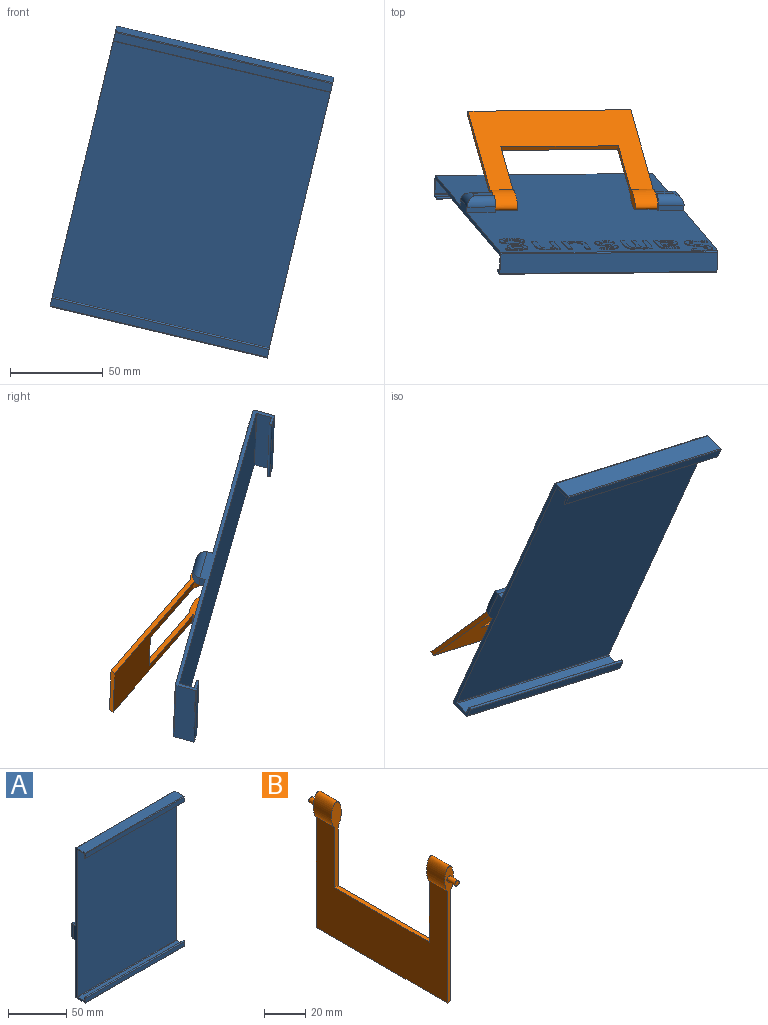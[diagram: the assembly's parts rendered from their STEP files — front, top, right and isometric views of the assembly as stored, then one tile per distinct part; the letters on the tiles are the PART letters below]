
ASSEMBLY  parts=2 mates=1
PART A: 200 faces, bbox 120x19.9x158 mm
  f0: plane 157.09x120mm, normal (0,1,0), area 17591.8mm2, adj f1,f2,f19,f20,f23,f24,f25,f26
  f1: plane 15.75x3mm, normal (0,0,1), area 47.3mm2, adj f0,f24,f29,f34
  f2: plane 15.75x3mm, normal (0,0,-1), area 47.3mm2, adj f0,f24,f29,f36
  f3: plane 9.25x5mm, normal (0,1,0), area 46.2mm2, adj f28,f37,f38,f39
  f4: plane 120x4.78mm, normal (0,-1,0), area 573.4mm2, adj f5,f22,f23,f24
  f5: cylinder r=0.88mm len=120mm, axis (-1,0,0), area 216.3mm2, adj f4,f6,f23,f24
  f6: plane 120x3.22mm, normal (0,1,0), area 386.9mm2, adj f5,f7,f23,f24
  f7: cylinder r=0.5mm len=120mm, axis (-1,0,0), area 94.2mm2, adj f6,f8,f23,f24
  f8: plane 120x7.4mm, normal (0,0,-1), area 888mm2, adj f7,f9,f23,f24
  f9: cylinder r=0.5mm len=120mm, axis (-1,0,0), area 94.2mm2, adj f8,f10,f23,f24
  f10: plane 154x120mm, normal (0,-1,0), area 18480mm2, adj f9,f11,f23,f24
  f11: cylinder r=0.5mm len=120mm, axis (-1,0,0), area 94.2mm2, adj f10,f12,f23,f24
  f12: plane 120x7.4mm, normal (0,0,1), area 888mm2, adj f11,f13,f23,f24
  f13: cylinder r=0.5mm len=120mm, axis (-1,0,0), area 94.2mm2, adj f12,f14,f23,f24
  f14: plane 120x3.02mm, normal (0,1,0), area 361.8mm2, adj f13,f15,f23,f24
  f15: cylinder r=0.76mm len=120mm, axis (-1,0,0), area 255mm2, adj f14,f16,f23,f24
  f16: plane 120x4.48mm, normal (0,-1,0), area 537.4mm2, adj f15,f17,f23,f24
  f17: cylinder r=0.5mm len=120mm, axis (-1,0,0), area 94.2mm2, adj f16,f18,f23,f24
  f18: plane 120x10.9mm, normal (0,0,-1), area 1308mm2, adj f17,f19,f23,f24
  f19: cylinder r=0.5mm len=120mm, axis (-1,0,0), area 94.2mm2, adj f0,f18,f23,f24
  f20: cylinder r=0.5mm len=120mm, axis (-1,0,0), area 94.2mm2, adj f0,f21,f23,f24,f61
  f21: plane 120x10.9mm, normal (0,0,1), area 1308mm2, adj f20,f22,f23,f24
  f22: cylinder r=0.5mm len=120mm, axis (-1,0,0), area 94.2mm2, adj f4,f21,f23,f24
  f23: plane 158x14.9mm, normal (1,0,0), area 402.7mm2, adj f0,f4,f5,f6,f7,f8,f9,f10
  f24: plane 158x14.9mm, normal (-1,0,0), area 402.7mm2, adj f0,f1,f2,f4,f5,f6,f7,f8
  f25: plane 14.25x3mm, normal (0,0,1), area 42.7mm2, adj f0,f23,f28,f37
  f26: plane 14.25x3mm, normal (0,0,-1), area 42.7mm2, adj f0,f23,f28,f39
  f27: plane 10.75x5mm, normal (0,1,0), area 53.8mm2, adj f29,f34,f35,f36
  f28: plane 15x8mm, normal (-1,0,0), area 99.6mm2, adj f0,f3,f25,f26,f30,f37,f39
  f29: plane 15x8mm, normal (1,0,0), area 99.6mm2, adj f0,f1,f2,f27,f32,f34,f36
  f30: cylinder r=1.75mm len=6mm, axis (-1,0,0), area 66mm2, adj f28,f31
  f31: plane 3.5x3.5mm, normal (-1,0,0), area 9.6mm2, adj f30
  f32: cylinder r=1.75mm len=6mm, axis (1,0,0), area 66mm2, adj f29,f33
  f33: plane 3.5x3.5mm, normal (1,0,0), area 9.6mm2, adj f32
  f34: cylinder r=5mm len=15.75mm, axis (-1,0,0), area 109.4mm2, adj f1,f27,f29,f35
  f35: cylinder r=5mm len=15mm, axis (0,0,1), area 89.3mm2, adj f24,f27,f34,f36
  f36: cylinder r=5mm len=15.75mm, axis (1,0,0), area 109.4mm2, adj f2,f27,f29,f35
  f37: cylinder r=5mm len=14.25mm, axis (-1,0,0), area 97.6mm2, adj f3,f25,f28,f38
  f38: cylinder r=5mm len=15mm, axis (0,0,-1), area 89.3mm2, adj f3,f23,f37,f39
  f39: cylinder r=5mm len=14.25mm, axis (1,0,0), area 97.6mm2, adj f3,f26,f28,f38
  f40: extruded ~4.8x1.34mm, area 2.5mm2, adj f0,f41,f59,f60,f61
  f41: extruded ~3.71x1.75mm, area 2.1mm2, adj f0,f40,f42,f60
  f42: extruded ~3.59x1.23mm, area 1.9mm2, adj f0,f41,f43,f60
  f43: extruded ~4.07x2.38mm, area 2.4mm2, adj f0,f42,f44,f60
  f44: extruded ~3.89x1.81mm, area 2.2mm2, adj f0,f43,f45,f60
  f45: extruded ~2.18x0.96mm, area 1.2mm2, adj f0,f44,f46,f60
  f46: extruded ~4.77x3.27mm, area 3.3mm2, adj f0,f45,f47,f60
  f47: extruded ~5.64x1.17mm, area 2.9mm2, adj f0,f46,f48,f60
  f48: plane 2.42x0.5mm, normal (1,0,0), area 1.2mm2, adj f0,f47,f49,f60
  f49: extruded ~5.64x0.94mm, area 2.9mm2, adj f0,f48,f50,f60
  f50: extruded ~5.36x1.49mm, area 2.8mm2, adj f0,f49,f51,f60
  f51: extruded ~4.11x1.89mm, area 2.3mm2, adj f0,f50,f52,f60
  f52: extruded ~3.28x1.12mm, area 1.8mm2, adj f0,f51,f53,f60
  f53: extruded ~4.47x2.47mm, area 2.6mm2, adj f0,f52,f54,f60
  f54: extruded ~3.69x1.81mm, area 2.1mm2, adj f0,f53,f55,f60
  f55: extruded ~2.23x0.89mm, area 1.2mm2, adj f0,f54,f56,f60
  f56: extruded ~3.99x2.85mm, area 2.8mm2, adj f0,f55,f57,f60
  f57: extruded ~4.9x1.06mm, area 2.5mm2, adj f0,f56,f58,f60
  f58: plane 2.24x0.87mm, normal (-0.93,0,-0.36), area 1.2mm2, adj f0,f57,f59,f60
  f59: extruded ~5.67x1.06mm, area 2.9mm2, adj f0,f40,f58,f60,f61
  f60: plane 20.48x12.89mm, normal (0,1,0), area 100mm2, adj f40,f41,f42,f43,f44,f45,f46,f47
  f61: plane 3.67x0.13mm, normal (0,-1,0), area 0.3mm2, adj f20,f40,f59
  f62: plane 2.21x0.5mm, normal (-0.04,0,-1), area 1.1mm2, adj f63,f85,f86,f87
  f63: plane 1.35x0.5mm, normal (1,0,0), area 0.7mm2, adj f62,f64,f86,f87
  f64: extruded ~3.13x1.19mm, area 1.7mm2, adj f63,f65,f86,f87
  f65: extruded ~3.19x1.11mm, area 1.7mm2, adj f64,f66,f86,f87
  f66: extruded ~2.72x2.42mm, area 2.1mm2, adj f65,f67,f86,f87
  f67: extruded ~2.23x1.12mm, area 1.3mm2, adj f66,f85,f86,f87
  f68: plane 2.07x0.51mm, normal (0.97,0,-0.24), area 1.1mm2, adj f0,f69,f84,f86
  f69: plane 1.78x0.5mm, normal (0,0,-1), area 0.9mm2, adj f0,f68,f70,f86
  f70: plane 10.25x0.5mm, normal (-1,0,0), area 5.1mm2, adj f0,f69,f71,f86
  f71: extruded ~3.8x1.38mm, area 2.1mm2, adj f0,f70,f72,f86
  f72: extruded ~4.47x1.19mm, area 2.4mm2, adj f0,f71,f73,f86
  f73: extruded ~5.22x1.31mm, area 2.7mm2, adj f0,f72,f74,f86
  f74: plane 1.87x0.86mm, normal (0.91,0,-0.42), area 1mm2, adj f0,f73,f75,f86
  f75: extruded ~4.47x1.12mm, area 2.3mm2, adj f0,f74,f76,f86
  f76: extruded ~3.32x3.22mm, area 2.7mm2, adj f0,f75,f77,f86
  f77: plane 0.94x0.5mm, normal (1,0,0), area 0.5mm2, adj f0,f76,f78,f86
  f78: plane 2.76x0.5mm, normal (0.03,0,1), area 1.4mm2, adj f0,f77,f79,f86
  f79: extruded ~6.95x4.74mm, area 4.7mm2, adj f0,f78,f80,f86
  f80: extruded ~3.28x1.26mm, area 1.8mm2, adj f0,f79,f81,f86
  f81: extruded ~3.48x1.17mm, area 1.9mm2, adj f0,f80,f82,f86
  f82: extruded ~2.85x0.51mm, area 1.5mm2, adj f0,f81,f83,f86
  f83: extruded ~2.15x1.83mm, area 1.4mm2, adj f0,f82,f84,f86
  f84: plane 0.5x0.11mm, normal (0,0,-1), area 0.1mm2, adj f0,f68,f83,f86
  f85: extruded ~3.79x0.84mm, area 2mm2, adj f62,f67,f86,f87
  f86: plane 15.51x12.14mm, normal (0,1,0), area 95.3mm2, adj f62,f63,f64,f65,f66,f67,f68,f69
  f87: plane 7.11x5.58mm, normal (0,1,0), area 32mm2, adj f62,f63,f64,f65,f66,f67,f85
  f88: plane 9.63x0.5mm, normal (1,0,0), area 4.8mm2, adj f0,f89,f112,f113
  f89: plane 2.21x0.5mm, normal (0,0,-1), area 1.1mm2, adj f0,f88,f90,f113
  f90: plane 9.77x0.5mm, normal (-1,0,0), area 4.9mm2, adj f0,f89,f91,f113
  f91: extruded ~4.2x0.79mm, area 2.2mm2, adj f0,f90,f92,f113
  f92: extruded ~2.53x1.26mm, area 1.5mm2, adj f0,f91,f93,f113
  f93: extruded ~2.98x2.48mm, area 2.1mm2, adj f0,f92,f94,f113
  f94: plane 0.5x0.08mm, normal (0,0,1), area 0mm2, adj f0,f93,f95,f113
  f95: extruded ~2.9x2.48mm, area 2.1mm2, adj f0,f94,f96,f113
  f96: extruded ~2.74x2.29mm, area 1.9mm2, adj f0,f95,f97,f113
  f97: plane 0.5x0.14mm, normal (0,0,1), area 0.1mm2, adj f0,f96,f98,f113
  f98: plane 2.01x0.5mm, normal (-0.98,0,0.18), area 1mm2, adj f0,f97,f99,f113
  f99: plane 1.73x0.5mm, normal (0,0,1), area 0.9mm2, adj f0,f98,f100,f113
  f100: plane 14.96x0.5mm, normal (1,0,0), area 7.5mm2, adj f0,f99,f101,f113
  f101: plane 2.21x0.5mm, normal (0,0,-1), area 1.1mm2, adj f0,f100,f102,f113
  f102: plane 7.75x0.5mm, normal (-1,0,0), area 3.9mm2, adj f0,f101,f103,f113
  f103: extruded ~4.34x0.5mm, area 2.2mm2, adj f0,f102,f104,f113
  f104: extruded ~1.63x1.08mm, area 1mm2, adj f0,f103,f105,f113
  f105: extruded ~3.54x1.7mm, area 2.2mm2, adj f0,f104,f106,f113
  f106: plane 9.63x0.5mm, normal (1,0,0), area 4.8mm2, adj f0,f105,f107,f113
  f107: plane 2.19x0.5mm, normal (0,0,-1), area 1.1mm2, adj f0,f106,f108,f113
  f108: plane 8.26x0.5mm, normal (-1,0,0), area 4.1mm2, adj f0,f107,f109,f113
  f109: extruded ~3.79x0.54mm, area 1.9mm2, adj f0,f108,f110,f113
  f110: extruded ~1.72x1.13mm, area 1.1mm2, adj f0,f109,f111,f113
  f111: extruded ~1.21x0.78mm, area 0.8mm2, adj f0,f110,f112,f113
  f112: extruded ~2.77x0.5mm, area 1.4mm2, adj f0,f88,f111,f113
  f113: plane 15.23x14.26mm, normal (0,1,0), area 111.6mm2, adj f88,f89,f90,f91,f92,f93,f94,f95
  f114: plane 2.26x0.5mm, normal (1,0,0), area 1.1mm2, adj f0,f115,f133,f134
  f115: extruded ~5.11x0.94mm, area 2.6mm2, adj f0,f114,f116,f134
  f116: extruded ~4.51x1.17mm, area 2.4mm2, adj f0,f115,f117,f134
  f117: extruded ~3.21x1.59mm, area 1.9mm2, adj f0,f116,f118,f134
  f118: extruded ~2.49x0.95mm, area 1.4mm2, adj f0,f117,f119,f134
  f119: extruded ~3.82x2.06mm, area 2.2mm2, adj f0,f118,f120,f134
  f120: extruded ~3.17x1.39mm, area 1.7mm2, adj f0,f119,f121,f134
  f121: extruded ~1.33x0.69mm, area 0.8mm2, adj f0,f120,f122,f134
  f122: extruded ~3.22x1.81mm, area 2.1mm2, adj f0,f121,f123,f134
  f123: extruded ~4.35x0.98mm, area 2.2mm2, adj f0,f122,f124,f134
  f124: plane 2.03x0.82mm, normal (-0.93,0,-0.37), area 1.1mm2, adj f0,f123,f125,f134
  f125: extruded ~5.03x1.01mm, area 2.6mm2, adj f0,f124,f126,f134
  f126: extruded ~4.21x1.06mm, area 2.2mm2, adj f0,f125,f127,f134
  f127: extruded ~2.91x1.52mm, area 1.7mm2, adj f0,f126,f128,f134
  f128: extruded ~2.33x0.83mm, area 1.3mm2, adj f0,f127,f129,f134
  f129: extruded ~4x2.17mm, area 2.3mm2, adj f0,f128,f130,f134
  f130: extruded ~3.08x1.44mm, area 1.7mm2, adj f0,f129,f131,f134
  f131: extruded ~1.35x0.67mm, area 0.8mm2, adj f0,f130,f132,f134
  f132: extruded ~3.75x2.21mm, area 2.4mm2, adj f0,f131,f133,f134
  f133: extruded ~5.04x1.17mm, area 2.6mm2, adj f0,f114,f132,f134
  f134: plane 15.51x11.21mm, normal (0,1,0), area 76.9mm2, adj f114,f115,f116,f117,f118,f119,f120,f121
  f135: plane 2x0.5mm, normal (0.98,0,-0.18), area 1mm2, adj f0,f136,f148,f149
  f136: plane 2.01x0.5mm, normal (0,0,-1), area 1mm2, adj f0,f135,f137,f149
  f137: plane 14.96x0.5mm, normal (-1,0,0), area 7.5mm2, adj f0,f136,f138,f149
  f138: plane 2.48x0.5mm, normal (0,0,1), area 1.2mm2, adj f0,f137,f139,f149
  f139: plane 7.76x0.5mm, normal (1,0,0), area 3.9mm2, adj f0,f138,f140,f149
  f140: extruded ~4.15x1.01mm, area 2.2mm2, adj f0,f139,f141,f149
  f141: extruded ~3.2x1.26mm, area 1.8mm2, adj f0,f140,f142,f149
  f142: extruded ~3.54x3.21mm, area 2.7mm2, adj f0,f141,f143,f149
  f143: plane 9.63x0.5mm, normal (-1,0,0), area 4.8mm2, adj f0,f142,f144,f149
  f144: plane 2.48x0.5mm, normal (0,0,1), area 1.2mm2, adj f0,f143,f145,f149
  f145: plane 9.77x0.5mm, normal (1,0,0), area 4.9mm2, adj f0,f144,f146,f149
  f146: extruded ~5.47x5.33mm, area 4.4mm2, adj f0,f145,f147,f149
  f147: extruded ~4.55x2.28mm, area 2.7mm2, adj f0,f146,f148,f149
  f148: plane 0.5x0.14mm, normal (0,0,-1), area 0.1mm2, adj f0,f135,f147,f149
  f149: plane 15.23x12.39mm, normal (0,1,0), area 87.3mm2, adj f135,f136,f137,f138,f139,f140,f141,f142
  f150: plane 9.63x0.5mm, normal (1,0,0), area 4.8mm2, adj f0,f151,f162,f163
  f151: plane 2.48x0.5mm, normal (0,0,-1), area 1.2mm2, adj f0,f150,f152,f163
  f152: plane 9.77x0.5mm, normal (-1,0,0), area 4.9mm2, adj f0,f151,f153,f163
  f153: extruded ~5.46x5.3mm, area 4.4mm2, adj f0,f152,f154,f163
  f154: extruded ~4.58x2.29mm, area 2.7mm2, adj f0,f153,f155,f163
  f155: plane 0.5x0.14mm, normal (0,0,1), area 0.1mm2, adj f0,f154,f156,f163
  f156: plane 2.01x0.5mm, normal (-0.98,0,0.18), area 1mm2, adj f0,f155,f157,f163
  f157: plane 2x0.5mm, normal (0,0,1), area 1mm2, adj f0,f156,f158,f163
  f158: plane 14.96x0.5mm, normal (1,0,0), area 7.5mm2, adj f0,f157,f159,f163
  f159: plane 2.48x0.5mm, normal (0,0,-1), area 1.2mm2, adj f0,f158,f160,f163
  f160: plane 7.75x0.5mm, normal (-1,0,0), area 3.9mm2, adj f0,f159,f161,f163
  f161: extruded ~5.42x4.18mm, area 3.9mm2, adj f0,f160,f162,f163
  f162: extruded ~3.54x3.24mm, area 2.8mm2, adj f0,f150,f161,f163
  f163: plane 15.23x12.39mm, normal (0,1,0), area 87.6mm2, adj f150,f151,f152,f153,f154,f155,f156,f157
  f164: plane 2.56x0.5mm, normal (0,0,-1), area 1.3mm2, adj f165,f196,f197,f198
  f165: extruded ~2.7x0.5mm, area 1.4mm2, adj f164,f166,f197,f198
  f166: extruded ~1.61x0.68mm, area 0.9mm2, adj f165,f167,f197,f198
  f167: extruded ~5.38x3.04mm, area 3.5mm2, adj f166,f168,f197,f198
  f168: extruded ~3.69x2.37mm, area 2.5mm2, adj f167,f196,f197,f198
  f169: extruded ~3.13x3.04mm, area 2.5mm2, adj f170,f194,f197,f199
  f170: extruded ~3.09x3.09mm, area 2.5mm2, adj f169,f171,f197,f199
  f171: extruded ~3.3x3.07mm, area 2.6mm2, adj f170,f194,f197,f199
  f172: plane 1.54x0.5mm, normal (-1,0,0), area 0.8mm2, adj f0,f173,f195,f197
  f173: plane 5.15x0.5mm, normal (0,0,1), area 2.6mm2, adj f0,f172,f174,f197
  f174: extruded ~2.04x0.5mm, area 1mm2, adj f0,f173,f175,f197
  f175: extruded ~4.14x1.34mm, area 2.2mm2, adj f0,f174,f176,f197
  f176: extruded ~3.82x1.45mm, area 2.1mm2, adj f0,f175,f177,f197
  f177: extruded ~2.54x0.69mm, area 1.3mm2, adj f0,f176,f178,f197
  f178: extruded ~1.91x1.67mm, area 1.3mm2, adj f0,f177,f179,f197
  f179: extruded ~2.62x1.81mm, area 1.7mm2, adj f0,f178,f180,f197
  f180: extruded ~2.1x1.31mm, area 1.3mm2, adj f0,f179,f181,f197
  f181: extruded ~3.68x3.27mm, area 2.7mm2, adj f0,f180,f182,f197
  f182: extruded ~3.07x1.55mm, area 1.8mm2, adj f0,f181,f183,f197
  f183: extruded ~4.51x1.1mm, area 2.4mm2, adj f0,f182,f184,f197
  f184: extruded ~7.7x5.14mm, area 5.3mm2, adj f0,f183,f185,f197
  f185: extruded ~3x1.25mm, area 1.7mm2, adj f0,f184,f186,f197
  f186: extruded ~3.63x1.05mm, area 1.9mm2, adj f0,f185,f187,f197
  f187: plane 2.55x0.5mm, normal (0,0,1), area 1.3mm2, adj f0,f186,f188,f197
  f188: extruded ~2.19x1.14mm, area 1.4mm2, adj f0,f187,f189,f197
  f189: extruded ~1.81x1.36mm, area 1.2mm2, adj f0,f188,f190,f197
  f190: extruded ~1.17x0.5mm, area 0.6mm2, adj f0,f189,f191,f197
  f191: extruded ~4.04x1.3mm, area 2.2mm2, adj f0,f190,f192,f197
  f192: extruded ~3.49x1.45mm, area 2mm2, adj f0,f191,f193,f197
  f193: extruded ~2.9x0.89mm, area 1.5mm2, adj f0,f192,f195,f197
  f194: extruded ~3.25x3.07mm, area 2.6mm2, adj f169,f171,f197,f199
  f195: plane 2.67x0.5mm, normal (-0.14,0,-0.99), area 1.3mm2, adj f0,f172,f193,f197
  f196: extruded ~3.13x2.7mm, area 2.4mm2, adj f164,f168,f197,f198
  f197: plane 21.94x13.95mm, normal (0,1,0), area 135.7mm2, adj f164,f165,f166,f167,f168,f169,f170,f171
  f198: plane 9.08x5.07mm, normal (0,1,0), area 39.5mm2, adj f164,f165,f166,f167,f168,f196
  f199: plane 6.39x6.13mm, normal (0,1,0), area 32.6mm2, adj f169,f170,f171,f194
PART B: 14 faces, bbox 6.8x100.5x80.9 mm
  f0: plane 90x2.5mm, normal (0,0,-1), area 225mm2, adj f1,f5,f6,f7
  f1: plane 80.47x6.81mm, normal (0,1,0), area 237.4mm2, adj f0,f6,f7,f9,f10
  f2: plane 50.47x6.81mm, normal (0,-1,0), area 169.4mm2, adj f3,f6,f7,f9
  f3: plane 65x2.5mm, normal (0,0,1), area 162.5mm2, adj f2,f4,f6,f7
  f4: plane 50.88x6mm, normal (0,1,0), area 161mm2, adj f3,f6,f7,f8
  f5: plane 80.88x6mm, normal (0,-1,0), area 228.9mm2, adj f0,f6,f7,f8,f12
  f6: plane 90x66.55mm, normal (1,0,0), area 3607.3mm2, adj f0,f1,f2,f3,f4,f5,f8,f9
  f7: plane 90x66.58mm, normal (-1,0,0), area 3606.8mm2, adj f0,f1,f2,f3,f4,f5,f8,f9
  f8: extruded ~14.33x12.5mm, area 394.8mm2, adj f4,f5,f6,f7
  f9: extruded ~14.51x12.5mm, area 408.9mm2, adj f1,f2,f6,f7
  f10: cylinder r=1.5mm len=5mm, axis (0,-1,0), area 47mm2, adj f1,f11
  f11: plane 2.99x2.99mm, normal (0,1,0), area 7mm2, adj f10
  f12: cylinder r=1.5mm len=5.5mm, axis (0,1,0), area 51.7mm2, adj f5,f13
  f13: plane 2.99x2.99mm, normal (0,-1,0), area 7mm2, adj f12
PLACE A rot(axis=(0.76,0.65,-0.06),20.4deg) t=(56.7,-51.5,0.68)mm
PLACE B rot(axis=(0.44,-0.22,0.87),93.6deg) t=(106.41,-15.79,-51.68)mm
MATE pin_slot B.f12 <-> A.f30  axis (0.97,0.01,-0.23) through (158.27,-42.35,-28.99)mm
